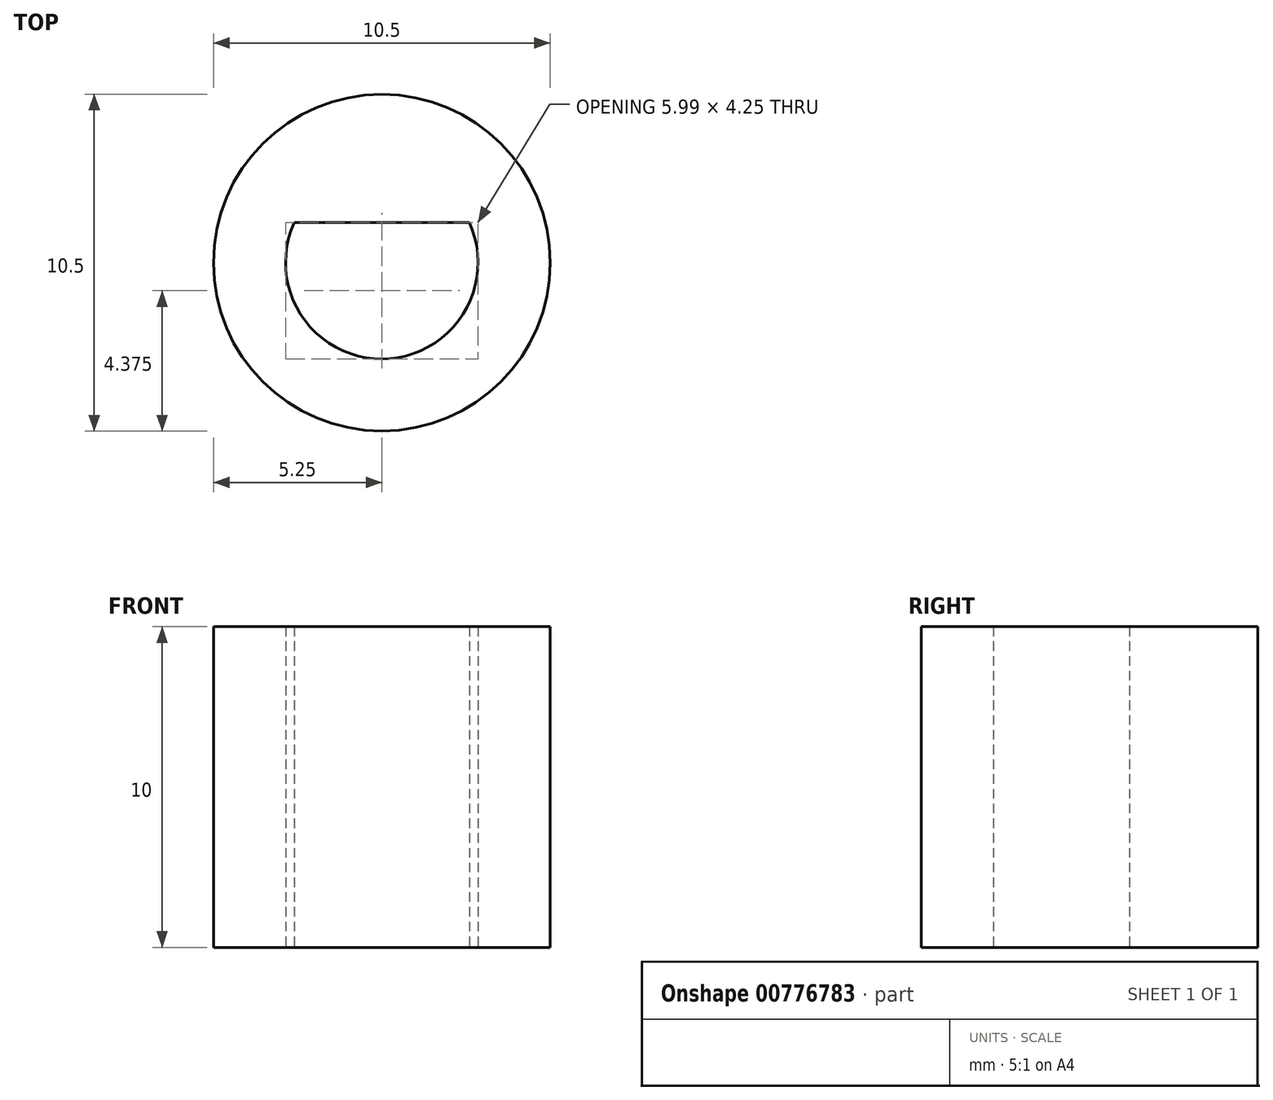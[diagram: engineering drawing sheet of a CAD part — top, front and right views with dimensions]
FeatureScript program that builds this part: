
annotation { "Feature Type Name" : "Feature", "Feature Type Description" : "" }
export const myFeature = defineFeature(function(context is Context, id is Id, definition is map)
    precondition{}
    {
        {
            var Q0;
            Q0=qCreatedBy(makeId("Top.planeOp"),FACE);
            var sketch = newSketch(context, id + "F0", { "sketchPlane" : qUnion([Q0])});
            skCircle(sketch, "E0", {"center": v(0, 0) * mm, "radius": 17.5 * mm});
            skCircle(sketch, "E1", {"center": v(0, 0) * mm, "radius": 5.25 * mm});
            skCircle(sketch, "E2", {"center": v(0, 0) * mm, "radius": 3 * mm});
            skLineSegment(sketch, "E3", {"start": v(-2.73, 1.25) * mm, "end": v(2.73, 1.25) * mm});
            skLineSegment(sketch, "E4", {"start": v(0, -22.5) * mm, "end": v(4, -17.04) * mm});
            skLineSegment(sketch, "E5", {"start": v(0, -22.5) * mm, "end": v(-4, -17.04) * mm});
            skSolve(sketch);
        }
        {
            var Q0;
            Q0=makeQuery(id+"F0.imprint","IMPRINT",FACE,{"disambiguationData":[TD([[makeQuery(id+"F0.imprint","IMPRINT",EDGE,{"derivedFrom":sQuery(id+"F0.wireOp",EDGE,"E1")}),1.0]])]});
            var Q1;
            {var subQ0=sQuery(id+"F0.wireOp",EDGE,"E3");Q1=makeQuery(id+"F0.imprint","IMPRINT",FACE,{"disambiguationData":[TD([[makeQuery(id+"F0.imprint","IMPRINT",EDGE,{"derivedFrom":subQ0}),1.0]])]});}
            extrude(context, id + "F1", {"entities" : qUnion([Q0, Q1]), "depth" : 10 * mm, "offsetDistance" : 25 * mm});
        }
    });
